# Revit family: TD92_TOC387_VER020_RVT20_R00
name_source: partatom
category: Mobiliário
units: mm (PartAtom-declared; Revit-internal decimal feet)

## family parameters
Com base no plano de trabalho = Não
Compartilhado = Não
Corte com vazios quando carregada = Não
Número OmniClass = 23.40.20.00
Ponto de cálculo do ambiente = Não
Sempre na vertical = Sim
Título OmniClass = General Furniture and Specialties

## types (1)
- TD92_TOC387_VER020_RVT20_R00
    Descrição = Garanta brincadeiras divertidas e seguras para os pequenos, com o Cercado Infantil Tramontina TocToc em Polietileno! Produzido em material super resistente, ele conta com 6 módulos encaixáveis, que permitem que você o monte de diversas formas, de acordo com o espaço disponível. Ele é indicado para crianças a partir de 3 anos e vai proporcionar a alegria e autonomia das crianças na medida certa e a segurança ideal para todos os momentos. Além disso, ele é leve, colorido, possui furos para fixação no chão e possibilita o encaixe do escorregador ZIP, acessório que vai deixar as brincadeiras da criançada muito mais especiais. Com a Tramontina, você tem as melhores opções para toda a sua família!
    Elevação padrão = 0  [stored 0 ft]
    Fabricante = Tramontina Delta S/A
    Modelo = Cercado Infantil Tramontina TocToc em Polietileno Verde
    Nota-chave = 92387020
    URL = https://www.tramontinastore.com

note: [stored X ft] marks values corroborated as IEEE doubles in the binary element streams (Revit-internal decimal feet)
